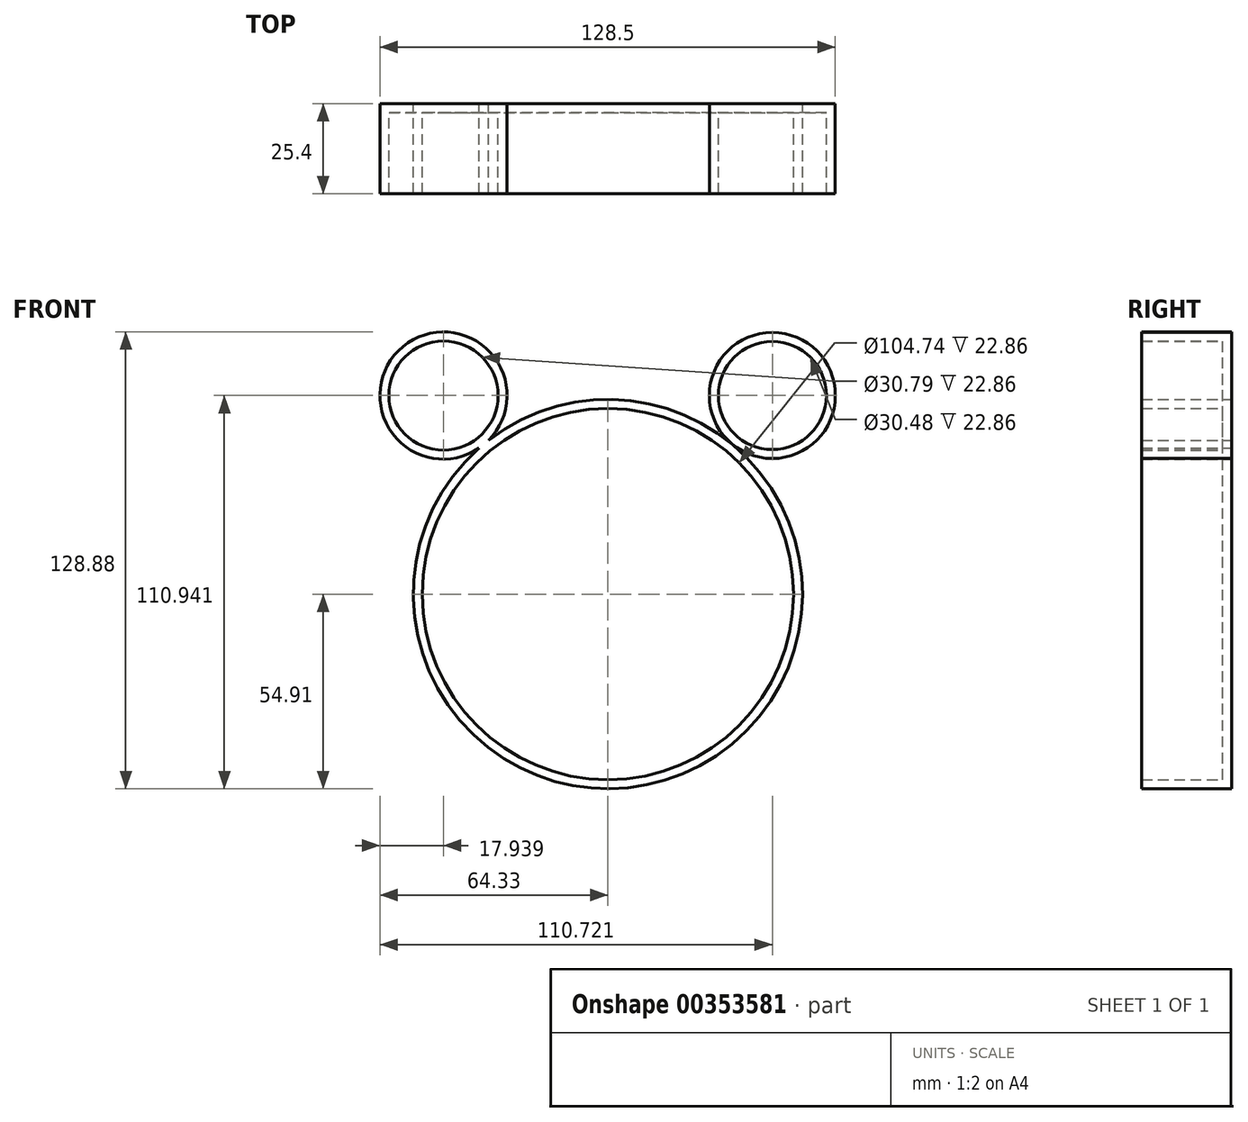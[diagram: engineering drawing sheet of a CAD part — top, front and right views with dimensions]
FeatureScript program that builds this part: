
annotation { "Feature Type Name" : "Feature", "Feature Type Description" : "" }
export const myFeature = defineFeature(function(context is Context, id is Id, definition is map)
    precondition{}
    {
        {
            var Q0;
            Q0=qCreatedBy(makeId("Front.planeOp"),FACE);
            var sketch = newSketch(context, id + "F0", { "sketchPlane" : qUnion([Q0])});
            skCircle(sketch, "E0", {"center": v(0, 0) * mm, "radius": 54.91 * mm});
            skCircle(sketch, "E1", {"center": v(-46.4, 56.03) * mm, "radius": 17.94 * mm});
            skCircle(sketch, "E2", {"center": v(46.4, 56.03) * mm, "radius": 17.78 * mm});
            skSolve(sketch);
        }
        {
            var Q0;
            Q0 = qSketchRegion(id + "F0", true);
            extrude(context, id + "F1", {"entities" : qUnion([Q0]), "depth" : 25.4 * mm, "offsetDistance" : 25.4 * mm});
        }
        {
            var Q0;
            Q0=makeQuery(id+"F1.opExtrude","CAP_FACE",FACE,{"disambiguationData":[OSD([sQuery(id+"F0.wireOp",EDGE,"E0"),sQuery(id+"F0.wireOp",EDGE,"E1")])],"isStart":false});
            var Q1;
            Q1=makeQuery(id+"F1.opExtrude","CAP_FACE",FACE,{"disambiguationData":[OSD([sQuery(id+"F0.wireOp",EDGE,"E2")])],"isStart":false});
            shell(context, id + "F2", {"entities" : qUnion([Q0, Q1]), "thickness" : 2.54 * mm});
        }
    });
